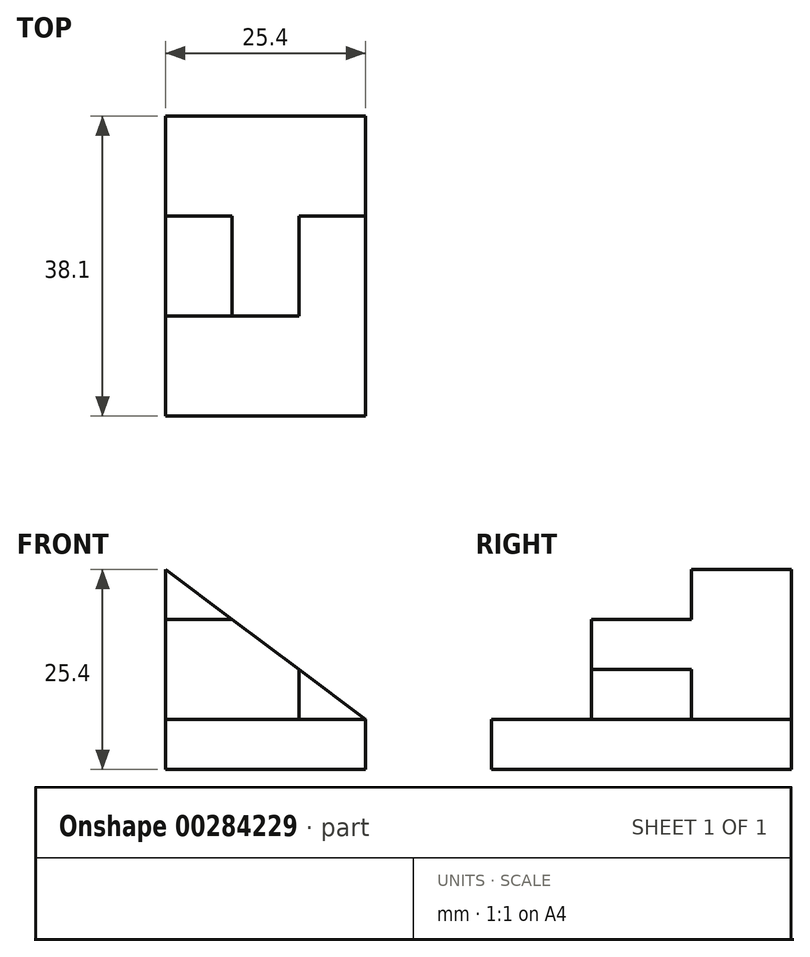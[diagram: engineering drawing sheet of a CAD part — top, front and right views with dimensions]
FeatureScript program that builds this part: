
annotation { "Feature Type Name" : "Feature", "Feature Type Description" : "" }
export const myFeature = defineFeature(function(context is Context, id is Id, definition is map)
    precondition{}
    {
        {
            var Q0;
            Q0=qCreatedBy(makeId("Front.planeOp"),FACE);
            var sketch = newSketch(context, id + "F0", { "sketchPlane" : qUnion([Q0])});
            skLineSegment(sketch, "E0", {"start": v(0, 0) * mm, "end": v(25.4, 0) * mm});
            skLineSegment(sketch, "E1", {"start": v(25.4, 0) * mm, "end": v(25.4, 6.35) * mm});
            skLineSegment(sketch, "E2", {"start": v(25.4, 6.35) * mm, "end": v(0, 25.4) * mm});
            skLineSegment(sketch, "E3", {"start": v(0, 25.4) * mm, "end": v(0, 0) * mm});
            skSolve(sketch);
        }
        {
            var Q0;
            Q0 = qSketchRegion(id + "F0", true);
            extrude(context, id + "F1", {"entities" : qUnion([Q0]), "depth" : 38.1 * mm});
        }
        {
            var Q0;
            Q0=makeQuery(id+"F1.opExtrude","CAP_FACE",FACE,{"disambiguationData":[OSD([sQuery(id+"F0.wireOp",EDGE,"E0"),sQuery(id+"F0.wireOp",EDGE,"E1"),sQuery(id+"F0.wireOp",EDGE,"E2"),sQuery(id+"F0.wireOp",EDGE,"E3")])],"isStart":false});
            var sketch = newSketch(context, id + "F2", { "sketchPlane" : qUnion([Q0])});
            skLineSegment(sketch, "E4", {"start": v(0, 25.4) * mm, "end": v(0, 19.05) * mm});
            skLineSegment(sketch, "E5", {"start": v(0, 19.05) * mm, "end": v(8.47, 19.05) * mm});
            skLineSegment(sketch, "E6", {"start": v(8.47, 19.05) * mm, "end": v(0, 25.4) * mm});
            skSolve(sketch);
        }
        {
            var Q0;
            Q0 = qSketchRegion(id + "F2", true);
            extrude(context, id + "F3", {"entities" : qUnion([Q0]), "operationType" : NewBodyOperationType.REMOVE, "oppositeDirection" : true, "depth" : 25.4 * mm});
        }
        {
            var Q0;
            Q0=makeQuery(id+"F1.opExtrude","CAP_FACE",FACE,{"disambiguationData":[OSD([sQuery(id+"F0.wireOp",EDGE,"E0"),sQuery(id+"F0.wireOp",EDGE,"E1"),sQuery(id+"F0.wireOp",EDGE,"E2"),sQuery(id+"F0.wireOp",EDGE,"E3")])],"isStart":false});
            var sketch = newSketch(context, id + "F4", { "sketchPlane" : qUnion([Q0])});
            skLineSegment(sketch, "E7", {"start": v(16.93, 12.7) * mm, "end": v(16.93, 6.35) * mm});
            skLineSegment(sketch, "E8", {"start": v(16.93, 6.35) * mm, "end": v(25.4, 6.35) * mm});
            skLineSegment(sketch, "E9", {"start": v(25.4, 6.35) * mm, "end": v(16.93, 12.7) * mm});
            skSolve(sketch);
        }
        {
            var Q0;
            Q0 = qSketchRegion(id + "F4", true);
            extrude(context, id + "F5", {"entities" : qUnion([Q0]), "operationType" : NewBodyOperationType.REMOVE, "oppositeDirection" : true, "depth" : 25.4 * mm});
        }
        {
            var Q0;
            Q0=makeQuery(id+"F1.opExtrude","CAP_FACE",FACE,{"disambiguationData":[OSD([sQuery(id+"F0.wireOp",EDGE,"E0"),sQuery(id+"F0.wireOp",EDGE,"E1"),sQuery(id+"F0.wireOp",EDGE,"E2"),sQuery(id+"F0.wireOp",EDGE,"E3")])],"isStart":false});
            var sketch = newSketch(context, id + "F6", { "sketchPlane" : qUnion([Q0])});
            skLineSegment(sketch, "E10", {"start": v(16.93, 6.35) * mm, "end": v(0, 6.35) * mm});
            skLineSegment(sketch, "E11", {"start": v(0, 6.35) * mm, "end": v(0, 19.05) * mm});
            skLineSegment(sketch, "E12", {"start": v(0, 19.05) * mm, "end": v(8.47, 19.05) * mm});
            skLineSegment(sketch, "E13", {"start": v(8.47, 19.05) * mm, "end": v(16.93, 12.7) * mm});
            skLineSegment(sketch, "E14", {"start": v(16.93, 12.7) * mm, "end": v(16.93, 6.35) * mm});
            skSolve(sketch);
        }
        {
            var Q0;
            Q0 = qSketchRegion(id + "F6", true);
            extrude(context, id + "F7", {"entities" : qUnion([Q0]), "operationType" : NewBodyOperationType.REMOVE, "oppositeDirection" : true, "depth" : 12.7 * mm});
        }
    });
